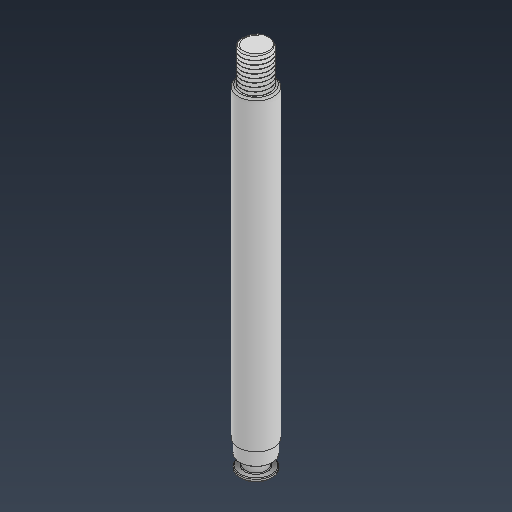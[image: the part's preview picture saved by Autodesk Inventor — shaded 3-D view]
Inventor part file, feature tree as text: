
AUTODESK INVENTOR PART (.ipt)
format: ipt  version: 2021 (Build 250183000, 183)  size: 246,784 bytes
history: native  units: in
note: dims shown in document units (in); Inventor stores cm internally (conversion verified against a paired STEP export)
features: chamfer x1
ambient origin geometry x8: Origin, YZ Plane, XZ Plane, XY Plane, X Axis, Y Axis, Z Axis, Center Point
bodies: Solid1 (feature_tree)
feature tree (1):
  chamfer  "Chamfer3"  [1 undecoded]
note: 1 required parameter value undecoded (feature->parameter linkage not recoverable at this tier; creation-order binding heuristic only, values carry confidence <= 0.55)
